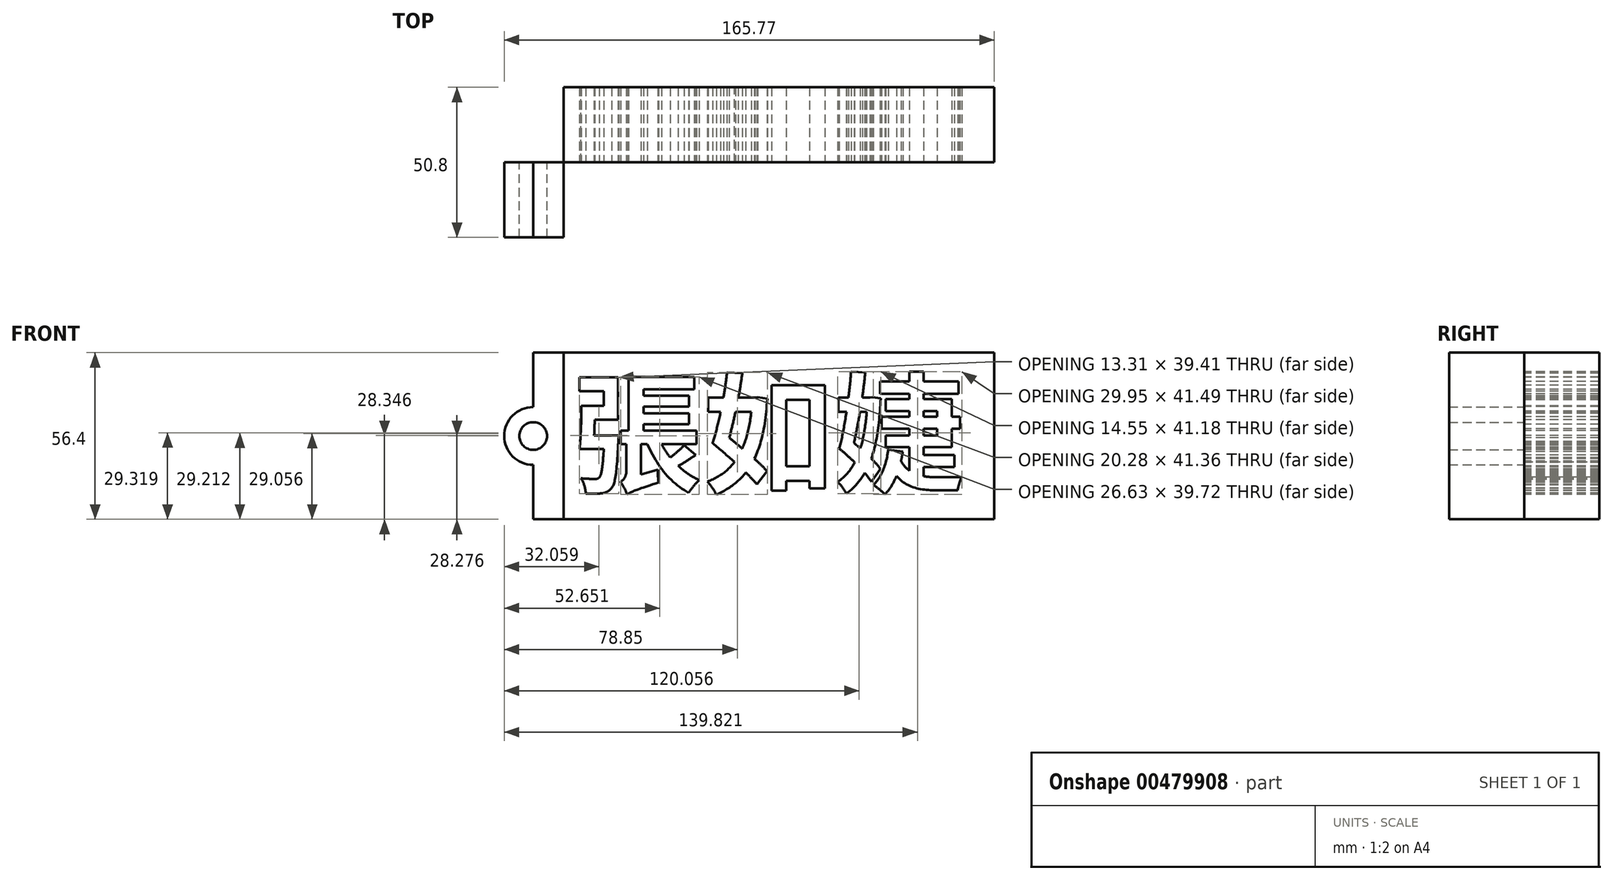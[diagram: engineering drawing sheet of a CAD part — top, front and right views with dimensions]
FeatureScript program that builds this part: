
annotation { "Feature Type Name" : "Feature", "Feature Type Description" : "" }
export const myFeature = defineFeature(function(context is Context, id is Id, definition is map)
    precondition{}
    {
        {
            var Q0;
            Q0=qCreatedBy(makeId("Front.planeOp"),FACE);
            var sketch = newSketch(context, id + "F0", { "sketchPlane" : qUnion([Q0])});
            skLineSegment(sketch, "E0.bottom", {"start": v(72.81, -28.2) * mm, "end": v(-72.81, -28.2) * mm});
            skLineSegment(sketch, "E0.top", {"start": v(72.81, 28.2) * mm, "end": v(-72.81, 28.2) * mm});
            skLineSegment(sketch, "E0.left", {"start": v(72.81, -28.2) * mm, "end": v(72.81, 28.2) * mm});
            skLineSegment(sketch, "E0.right", {"start": v(-72.81, -28.2) * mm, "end": v(-72.81, 28.2) * mm});
            skPoint(sketch, "E0.middle", {"position": v(0, 0) * mm});
            skSolve(sketch);
        }
        {
            var Q0;
            Q0 = qSketchRegion(id + "F0", true);
            extrude(context, id + "F1", {"entities" : qUnion([Q0]), "depth" : 25.4 * mm});
        }
        {
            var Q0;
            Q0=makeQuery(id+"F1.opExtrude","CAP_FACE",FACE,{"disambiguationData":[OSD([sQuery(id+"F0.wireOp",EDGE,"E0.bottom"),sQuery(id+"F0.wireOp",EDGE,"E0.top"),sQuery(id+"F0.wireOp",EDGE,"E0.left"),sQuery(id+"F0.wireOp",EDGE,"E0.right")])],"isStart":false});
            var sketch = newSketch(context, id + "F2", { "sketchPlane" : qUnion([Q0])});
            skText(sketch, "E1", { "text": "張如婕", "fontName": "NotoSansCJKsc-Bold.otf"});
            const initialGuessF2  = {"E1": [-0.07022, -0.01583, 1, 0, 0.03195]};
            skSetInitialGuess(sketch, initialGuessF2);
            skSolve(sketch);
        }
        {
            var Q0;
            Q0 = qSketchRegion(id + "F2", true);
            extrude(context, id + "F3", {"entities" : qUnion([Q0]), "operationType" : NewBodyOperationType.REMOVE, "oppositeDirection" : true, "depth" : 25.4 * mm});
        }
        {
            var Q0;
            {var subQ0=sQuery(id+"F0.wireOp",EDGE,"E0.top");var subQ1=sQuery(id+"F0.wireOp",EDGE,"E0.right");var subQ2=sQuery(id+"F0.wireOp",EDGE,"E0.bottom");var subQ3=sQuery(id+"F0.wireOp",EDGE,"E0.left");Q0=makeQuery(id+"F3.boolean.opBoolean","SPLIT",FACE,{"disambiguationData":[TD([makeQuery(id+"F1.opExtrude","SWEPT_FACE",FACE,{"disambiguationData":[OSD([subQ2])]})])],"derivedFrom":makeQuery(id+"F1.opExtrude","CAP_FACE",FACE,{"disambiguationData":[OSD([subQ2,subQ0,subQ3,subQ1])],"isStart":false})});}
            var sketch = newSketch(context, id + "F4", { "sketchPlane" : qUnion([Q0])});
            skLineSegment(sketch, "E2.bottom", {"start": v(-72.81, 28.2) * mm, "end": v(-83.18, 28.2) * mm});
            skLineSegment(sketch, "E2.top", {"start": v(-72.81, -28.2) * mm, "end": v(-83.18, -28.2) * mm});
            skLineSegment(sketch, "E2.left", {"start": v(-72.81, 28.2) * mm, "end": v(-72.81, -28.2) * mm});
            skLineSegment(sketch, "E2.right", {"start": v(-83.18, 28.2) * mm, "end": v(-83.18, -28.2) * mm});
            skCircle(sketch, "E3", {"center": v(-83.18, 0) * mm, "radius": 9.79 * mm});
            skCircle(sketch, "E4", {"center": v(-83.18, 0) * mm, "radius": 4.69 * mm});
            skSolve(sketch);
        }
        {
            var Q0;
            Q0 = qSketchRegion(id + "F4", true);
            extrude(context, id + "F5", {"entities" : qUnion([Q0]), "depth" : 25.4 * mm});
        }
        {
            var Q0;
            Q0 = qSketchRegion(id + "F4", true);
            extrude(context, id + "F6", {"entities" : qUnion([Q0]), "operationType" : NewBodyOperationType.ADD, "depth" : 25.4 * mm});
        }
    });
